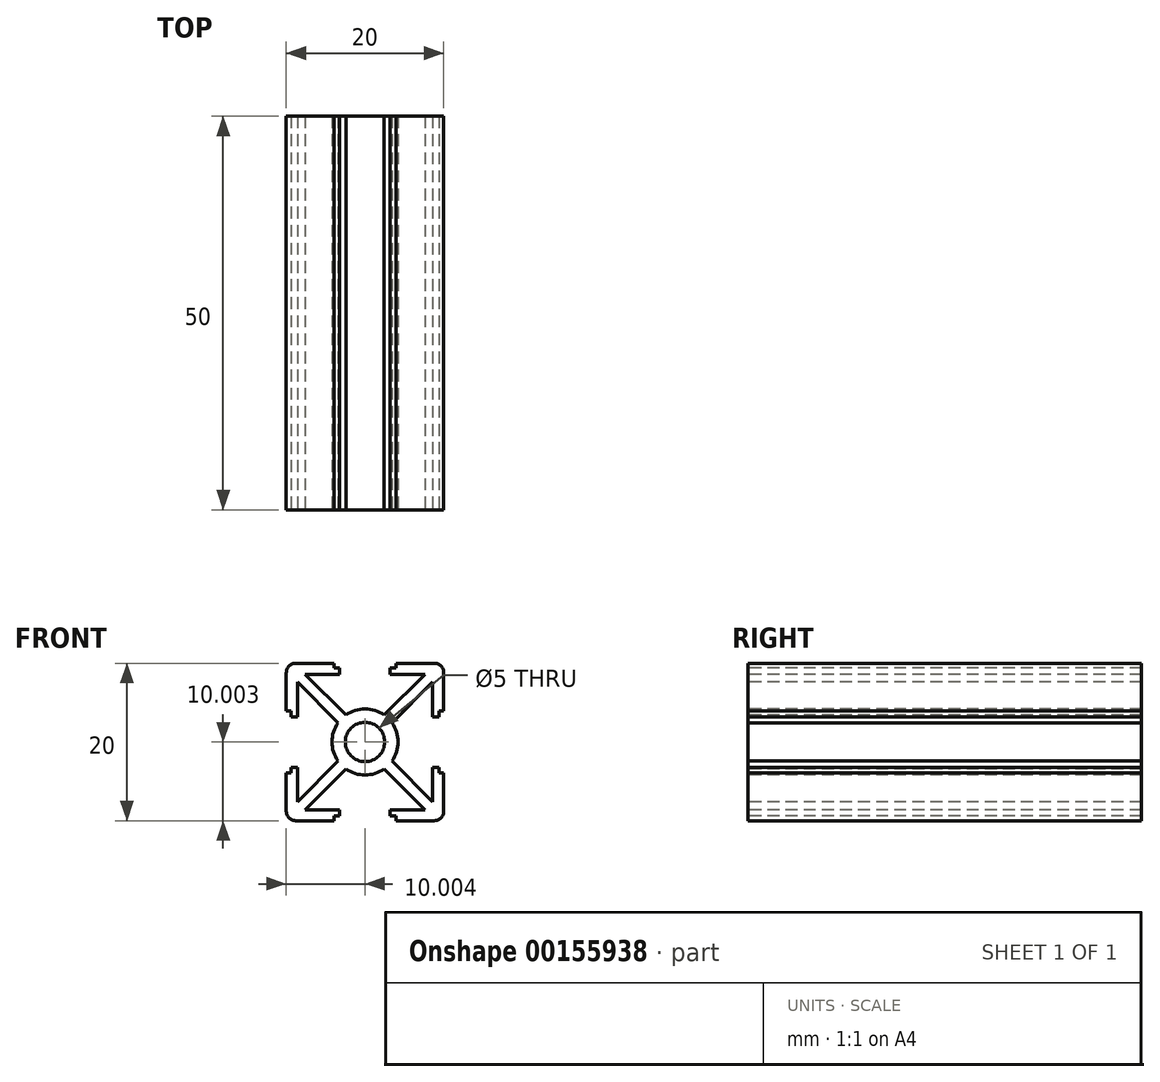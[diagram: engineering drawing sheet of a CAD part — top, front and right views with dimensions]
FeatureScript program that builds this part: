
annotation { "Feature Type Name" : "Feature", "Feature Type Description" : "" }
export const myFeature = defineFeature(function(context is Context, id is Id, definition is map)
    precondition{}
    {
        {
            var Q0;
            Q0=qCreatedBy(makeId("Front.planeOp"),FACE);
            var sketch = newSketch(context, id + "F0", { "sketchPlane" : qUnion([Q0])});
            skArc(sketch, "E0", {"start": v(-44.98, 42.64) * mm, "mid": v(-45.76, 40.2) * mm, "end": v(-44.98, 37.77) * mm});
            skCircle(sketch, "E1", {"center": v(-41.56, 40.2) * mm, "radius": 2.5 * mm});
            skLineSegment(sketch, "E2", {"start": v(-54.61, 53.26) * mm, "end": v(-41.56, 40.2) * mm, "construction": true});
            skLineSegment(sketch, "E3", {"start": v(-41.56, 40.2) * mm, "end": v(-28.67, 27.32) * mm, "construction": true});
            skLineSegment(sketch, "E4", {"start": v(-41.56, 40.2) * mm, "end": v(-29.82, 51.94) * mm, "construction": true});
            skLineSegment(sketch, "E5", {"start": v(-41.56, 40.2) * mm, "end": v(-53.14, 28.61) * mm, "construction": true});
            skLineSegment(sketch, "E6", {"start": v(-55.54, 40.2) * mm, "end": v(-21.72, 40.2) * mm, "construction": true});
            skLineSegment(sketch, "E7", {"start": v(-41.56, 50.17) * mm, "end": v(-41.56, 24.27) * mm, "construction": true});
            skLineSegment(sketch, "E8", {"start": v(-50.36, 50.2) * mm, "end": v(-45.5, 50.2) * mm});
            skLineSegment(sketch, "E9", {"start": v(-44.76, 49.6) * mm, "end": v(-44.76, 48.8) * mm});
            skLineSegment(sketch, "E10", {"start": v(-49.17, 48.8) * mm, "end": v(-43.99, 43.63) * mm});
            skLineSegment(sketch, "E11", {"start": v(-44.76, 48.8) * mm, "end": v(-49.17, 48.8) * mm});
            skLineSegment(sketch, "E12", {"start": v(-45.5, 50.2) * mm, "end": v(-45.5, 49.6) * mm});
            skLineSegment(sketch, "E13", {"start": v(-45.5, 49.6) * mm, "end": v(-44.76, 49.6) * mm});
            skPoint(sketch, "E14.orphan", {"position": v(-44.76, 50.2) * mm});
            skLineSegment(sketch, "E15.MirrorCS", {"start": v(-50.16, 47.81) * mm, "end": v(-44.98, 42.64) * mm});
            skLineSegment(sketch, "E16.MirrorCS", {"start": v(-50.16, 43.4) * mm, "end": v(-50.16, 47.81) * mm});
            skLineSegment(sketch, "E17.MirrorCS", {"start": v(-50.95, 43.4) * mm, "end": v(-50.16, 43.4) * mm});
            skLineSegment(sketch, "E18.MirrorCS", {"start": v(-50.95, 44.15) * mm, "end": v(-50.95, 43.4) * mm});
            skLineSegment(sketch, "E19.MirrorCS", {"start": v(-51.56, 49) * mm, "end": v(-51.56, 44.15) * mm});
            skLineSegment(sketch, "E20.MirrorCS", {"start": v(-51.56, 44.15) * mm, "end": v(-50.95, 44.15) * mm});
            skLineSegment(sketch, "E21.MirrorCS", {"start": v(-32.96, 47.81) * mm, "end": v(-38.13, 42.64) * mm});
            skLineSegment(sketch, "E22.MirrorCS", {"start": v(-33.95, 48.8) * mm, "end": v(-39.12, 43.63) * mm});
            skLineSegment(sketch, "E23.MirrorCS", {"start": v(-37.6, 49.6) * mm, "end": v(-38.36, 49.6) * mm});
            skLineSegment(sketch, "E24.MirrorCS", {"start": v(-32.16, 44.15) * mm, "end": v(-32.16, 43.4) * mm});
            skLineSegment(sketch, "E25.MirrorCS", {"start": v(-31.56, 44.15) * mm, "end": v(-32.16, 44.15) * mm});
            skLineSegment(sketch, "E26.MirrorCS", {"start": v(-38.36, 49.6) * mm, "end": v(-38.36, 48.8) * mm});
            skLineSegment(sketch, "E27.MirrorCS", {"start": v(-37.6, 50.2) * mm, "end": v(-37.6, 49.6) * mm});
            skLineSegment(sketch, "E28.MirrorCS", {"start": v(-32.16, 43.4) * mm, "end": v(-32.96, 43.4) * mm});
            skLineSegment(sketch, "E29.MirrorCS", {"start": v(-32.96, 43.4) * mm, "end": v(-32.96, 47.81) * mm});
            skPoint(sketch, "E30.MirrorP", {"position": v(-38.36, 50.2) * mm});
            skLineSegment(sketch, "E31.MirrorCS", {"start": v(-38.36, 48.8) * mm, "end": v(-33.95, 48.8) * mm});
            skLineSegment(sketch, "E32.MirrorCS", {"start": v(-32.76, 50.2) * mm, "end": v(-37.6, 50.2) * mm});
            skLineSegment(sketch, "E33.MirrorCS", {"start": v(-31.56, 49) * mm, "end": v(-31.56, 44.15) * mm});
            skLineSegment(sketch, "E34.MirrorCS", {"start": v(-32.16, 37) * mm, "end": v(-32.96, 37) * mm});
            skLineSegment(sketch, "E35.MirrorCS", {"start": v(-38.36, 30.8) * mm, "end": v(-38.36, 31.6) * mm});
            skLineSegment(sketch, "E36.MirrorCS", {"start": v(-32.16, 36.25) * mm, "end": v(-32.16, 37) * mm});
            skLineSegment(sketch, "E37.MirrorCS", {"start": v(-37.6, 30.8) * mm, "end": v(-38.36, 30.8) * mm});
            skLineSegment(sketch, "E38.MirrorCS", {"start": v(-31.56, 36.25) * mm, "end": v(-32.16, 36.25) * mm});
            skLineSegment(sketch, "E39.MirrorCS", {"start": v(-37.6, 30.2) * mm, "end": v(-37.6, 30.8) * mm});
            skLineSegment(sketch, "E40.MirrorCS", {"start": v(-32.76, 30.2) * mm, "end": v(-37.6, 30.2) * mm});
            skLineSegment(sketch, "E41.MirrorCS", {"start": v(-31.56, 31.4) * mm, "end": v(-31.56, 36.25) * mm});
            skLineSegment(sketch, "E42.MirrorCS", {"start": v(-33.95, 31.6) * mm, "end": v(-39.12, 36.78) * mm});
            skLineSegment(sketch, "E43.MirrorCS", {"start": v(-32.96, 37) * mm, "end": v(-32.96, 32.6) * mm});
            skPoint(sketch, "E44.MirrorP", {"position": v(-38.36, 30.2) * mm});
            skLineSegment(sketch, "E45.MirrorCS", {"start": v(-38.36, 31.6) * mm, "end": v(-33.95, 31.6) * mm});
            skLineSegment(sketch, "E46.MirrorCS", {"start": v(-32.96, 32.6) * mm, "end": v(-38.13, 37.77) * mm});
            skLineSegment(sketch, "E47.MirrorCS", {"start": v(-45.5, 30.8) * mm, "end": v(-44.76, 30.8) * mm});
            skLineSegment(sketch, "E48.MirrorCS", {"start": v(-51.56, 36.25) * mm, "end": v(-50.95, 36.25) * mm});
            skLineSegment(sketch, "E49.MirrorCS", {"start": v(-50.95, 36.25) * mm, "end": v(-50.95, 37) * mm});
            skLineSegment(sketch, "E50.MirrorCS", {"start": v(-50.95, 37) * mm, "end": v(-50.16, 37) * mm});
            skLineSegment(sketch, "E51.MirrorCS", {"start": v(-45.5, 30.2) * mm, "end": v(-45.5, 30.8) * mm});
            skLineSegment(sketch, "E52.MirrorCS", {"start": v(-44.76, 30.8) * mm, "end": v(-44.76, 31.6) * mm});
            skLineSegment(sketch, "E53.MirrorCS", {"start": v(-50.16, 37) * mm, "end": v(-50.16, 32.6) * mm});
            skLineSegment(sketch, "E54.MirrorCS", {"start": v(-50.16, 32.6) * mm, "end": v(-44.98, 37.77) * mm});
            skLineSegment(sketch, "E55.MirrorCS", {"start": v(-50.36, 30.2) * mm, "end": v(-45.5, 30.2) * mm});
            skPoint(sketch, "E56.MirrorP", {"position": v(-44.76, 30.2) * mm});
            skLineSegment(sketch, "E57.MirrorCS", {"start": v(-51.56, 31.4) * mm, "end": v(-51.56, 36.25) * mm});
            skLineSegment(sketch, "E58.MirrorCS", {"start": v(-49.17, 31.6) * mm, "end": v(-43.99, 36.78) * mm});
            skLineSegment(sketch, "E59.MirrorCS", {"start": v(-44.76, 31.6) * mm, "end": v(-49.17, 31.6) * mm});
            skPoint(sketch, "E60.visualSharp", {"position": v(-51.56, 50.2) * mm});
            skArc(sketch, "E60.filletArc", {"start": v(-50.36, 50.2) * mm, "mid": v(-51.2, 49.85) * mm, "end": v(-51.56, 49) * mm});
            skPoint(sketch, "E61.visualSharp", {"position": v(-31.56, 50.2) * mm});
            skArc(sketch, "E61.filletArc", {"start": v(-31.56, 49) * mm, "mid": v(-31.9, 49.85) * mm, "end": v(-32.76, 50.2) * mm});
            skPoint(sketch, "E62.visualSharp", {"position": v(-31.56, 30.2) * mm});
            skArc(sketch, "E62.filletArc", {"start": v(-32.76, 30.2) * mm, "mid": v(-31.9, 30.55) * mm, "end": v(-31.56, 31.4) * mm});
            skPoint(sketch, "E63.visualSharp", {"position": v(-51.56, 30.2) * mm});
            skArc(sketch, "E63.filletArc", {"start": v(-51.56, 31.4) * mm, "mid": v(-51.2, 30.55) * mm, "end": v(-50.36, 30.2) * mm});
            skArc(sketch, "E64.trimOffspring", {"start": v(-39.12, 43.63) * mm, "mid": v(-41.56, 44.4) * mm, "end": v(-43.99, 43.63) * mm});
            skArc(sketch, "E65.trimOffspring", {"start": v(-43.99, 36.78) * mm, "mid": v(-41.56, 36) * mm, "end": v(-39.12, 36.78) * mm});
            skArc(sketch, "E66.trimOffspring", {"start": v(-38.13, 37.77) * mm, "mid": v(-37.36, 40.2) * mm, "end": v(-38.13, 42.64) * mm});
            skSolve(sketch);
        }
        {
            var Q0;
            Q0=makeQuery(id+"F0.imprint","IMPRINT",FACE,{"disambiguationData":[TD([[makeQuery(id+"F0.imprint","IMPRINT",EDGE,{"derivedFrom":sQuery(id+"F0.wireOp",EDGE,"E0")}),1.0]])]});
            extrude(context, id + "F1", {"entities" : qUnion([Q0]), "oppositeDirection" : true, "depth" : 50 * mm});
        }
    });
